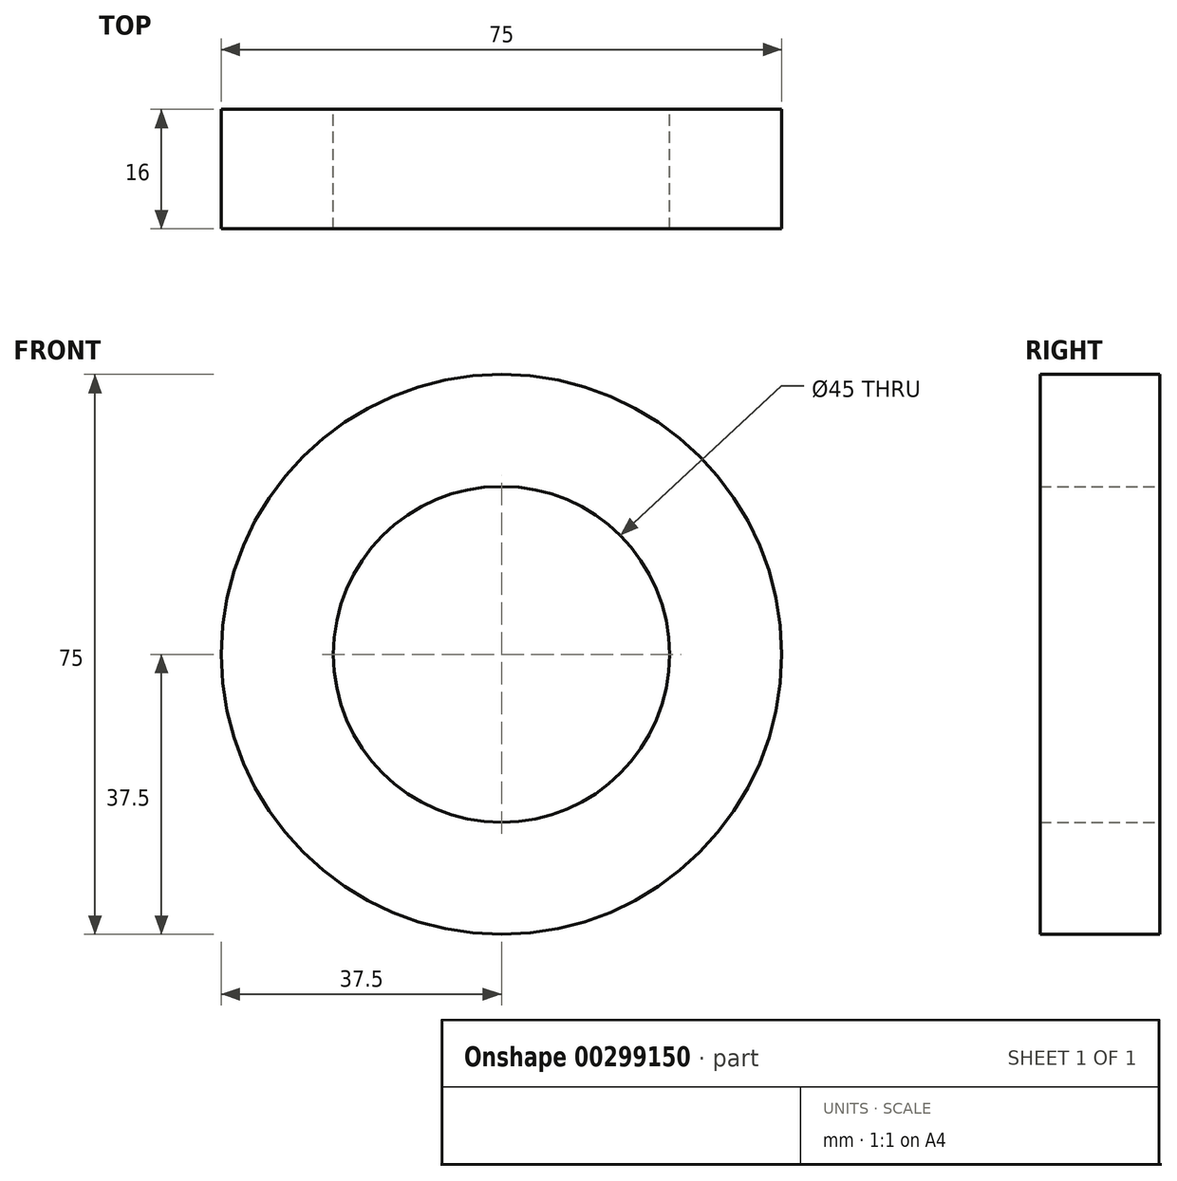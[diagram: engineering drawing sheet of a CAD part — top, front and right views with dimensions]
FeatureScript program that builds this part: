
annotation { "Feature Type Name" : "Feature", "Feature Type Description" : "" }
export const myFeature = defineFeature(function(context is Context, id is Id, definition is map)
    precondition{}
    {
        {
            var Q0;
            Q0=qCreatedBy(makeId("Front.planeOp"),FACE);
            var sketch = newSketch(context, id + "F0", { "sketchPlane" : qUnion([Q0])});
            skCircle(sketch, "E0", {"center": v(0, 0) * mm, "radius": 37.5 * mm});
            skCircle(sketch, "E1", {"center": v(0, 0) * mm, "radius": 22.5 * mm});
            skSolve(sketch);
        }
        {
            var Q0;
            Q0 = qSketchRegion(id + "F0", true);
            extrude(context, id + "F1", {"entities" : qUnion([Q0]), "depth" : 16 * mm});
        }
    });
